FCSTD DOCUMENT  (FreeCAD 1.0R39319 (Git))
Label: Week1Sketch2
License: All rights reserved
LicenseURL: https://en.wikipedia.org/wiki/All_rights_reserved
objects: Sketcher::SketchObject×1, PartDesign::Body×1
note: 3 computed .brp shape members not serialized (recipe doc carries the construction recipe); baked Part::Feature solids carry a one-line shape summary decoded from their .brp

FEATURE [Sketcher::SketchObject] Sketch
  ArcFitTolerance = 1e-06
  AttachmentSupport = -> [XY_Plane]
  FullyConstrained = true
  MakeInternals = false
  MapMode = 5
  sketch-geometry (30):
    g0: ArcOfCircle CenterX=0 CenterY=0 CenterZ=0 NormalX=0 NormalY=0 NormalZ=1 AngleXU=0 Radius=55 StartAngle=0.182835 EndAngle=1.38796
    g1: ArcOfCircle CenterX=-112.5 CenterY=0 CenterZ=0 NormalX=0 NormalY=0 NormalZ=1 AngleXU=0 Radius=26 StartAngle=0.394791 EndAngle=5.88839
    g2: ArcOfCircle CenterX=112.5 CenterY=0 CenterZ=0 NormalX=0 NormalY=0 NormalZ=1 AngleXU=0 Radius=26 StartAngle=3.53638 EndAngle=9.02999
    g3: Circle [constr] CenterX=0 CenterY=0 CenterZ=0 NormalX=0 NormalY=0 NormalZ=1 AngleXU=0 Radius=112.5
    g4: ArcOfCircle CenterX=0 CenterY=112.5 CenterZ=0 NormalX=0 NormalY=0 NormalZ=1 AngleXU=0 Radius=26 StartAngle=5.10718 EndAngle=10.6008
    g5: ArcOfCircle CenterX=0 CenterY=-112.5 CenterZ=0 NormalX=0 NormalY=0 NormalZ=1 AngleXU=0 Radius=26 StartAngle=1.96559 EndAngle=7.45919
    g6: LineSegment StartX=-130.885 StartY=18.3848 StartZ=0 EndX=-18.3848 EndY=130.885 EndZ=0
    g7: LineSegment StartX=18.3848 StartY=130.885 StartZ=0 EndX=130.885 EndY=18.3848 EndZ=0
    g8: Circle CenterX=-112.5 CenterY=0 CenterZ=0 NormalX=0 NormalY=0 NormalZ=1 AngleXU=0 Radius=20
    g9: Circle CenterX=0 CenterY=112.5 CenterZ=0 NormalX=0 NormalY=0 NormalZ=1 AngleXU=0 Radius=20
    g10: Circle CenterX=112.5 CenterY=0 CenterZ=0 NormalX=0 NormalY=0 NormalZ=1 AngleXU=0 Radius=20
    g11: Circle CenterX=0 CenterY=-112.5 CenterZ=0 NormalX=0 NormalY=0 NormalZ=1 AngleXU=0 Radius=20
    g12: Circle CenterX=0 CenterY=0 CenterZ=0 NormalX=0 NormalY=0 NormalZ=1 AngleXU=0 Radius=44
    g13: LineSegment StartX=-95.1795 StartY=10 StartZ=0 EndX=-42.8486 EndY=10 EndZ=0
    g14: LineSegment StartX=-95.1795 StartY=-10 StartZ=0 EndX=-42.8486 EndY=-10 EndZ=0
    g15: LineSegment StartX=-10 StartY=95.1795 StartZ=0 EndX=-10 EndY=42.8486 EndZ=0
    g16: LineSegment StartX=10 StartY=95.1795 StartZ=0 EndX=10 EndY=42.8486 EndZ=0
    g17: LineSegment StartX=-10 StartY=-95.1795 StartZ=0 EndX=-10 EndY=-42.8486 EndZ=0
    g18: LineSegment StartX=10 StartY=-95.1795 StartZ=0 EndX=10 EndY=-42.8486 EndZ=0
    g19: LineSegment StartX=95.1795 StartY=10 StartZ=0 EndX=42.8486 EndY=10 EndZ=0
    g20: LineSegment StartX=95.1795 StartY=-10 StartZ=0 EndX=42.8486 EndY=-10 EndZ=0
    g21: ArcOfCircle CenterX=0 CenterY=0 CenterZ=0 NormalX=0 NormalY=0 NormalZ=1 AngleXU=0 Radius=55 StartAngle=1.75363 EndAngle=2.95876
    g22: ArcOfCircle CenterX=0 CenterY=0 CenterZ=0 NormalX=0 NormalY=0 NormalZ=1 AngleXU=0 Radius=55 StartAngle=3.32443 EndAngle=4.52955
    g23: ArcOfCircle CenterX=0 CenterY=0 CenterZ=0 NormalX=0 NormalY=0 NormalZ=1 AngleXU=0 Radius=55 StartAngle=4.89522 EndAngle=6.10035
    g24: ArcOfCircle CenterX=-84.9611 CenterY=-59.9801 CenterZ=0 NormalX=0 NormalY=0 NormalZ=1 AngleXU=0 Radius=40 StartAngle=0.614722 EndAngle=2.00122
    g25: ArcOfCircle CenterX=0 CenterY=0 CenterZ=0 NormalX=0 NormalY=0 NormalZ=1 AngleXU=0 Radius=64 StartAngle=3.75631 EndAngle=4.09767
    g26: ArcOfCircle CenterX=-59.9801 CenterY=-84.9611 CenterZ=0 NormalX=0 NormalY=0 NormalZ=1 AngleXU=0 Radius=40 StartAngle=5.85276 EndAngle=7.23926
    g27: ArcOfCircle CenterX=84.9611 CenterY=-59.9801 CenterZ=0 NormalX=0 NormalY=0 NormalZ=1 AngleXU=0 Radius=40 StartAngle=1.14037 EndAngle=2.52687
    g28: ArcOfCircle CenterX=0 CenterY=0 CenterZ=0 NormalX=0 NormalY=0 NormalZ=1 AngleXU=0 Radius=64 StartAngle=5.32711 EndAngle=5.66846
    g29: ArcOfCircle CenterX=59.9801 CenterY=-84.9611 CenterZ=0 NormalX=0 NormalY=0 NormalZ=1 AngleXU=0 Radius=40 StartAngle=2.18552 EndAngle=3.57202
  constraints (96):
    c: Coincident(g0,g-1)
    c: PointOnObject(g1,g-1)
    c: Diameter(g0) = 110
    c: Diameter(g1) = 52
    c: Equal(g1,g2)
    c: Coincident(g3,g0)
    c: Diameter(g3) = 225
    c: PointOnObject(g1,g3)
    c: PointOnObject(g2,g3)
    c: PointOnObject(g4,g-2)
    c: PointOnObject(g5,g-2)
    c: Equal(g1,g4)
    c: Equal(g4,g5)
    c: PointOnObject(g4,g3)
    c: PointOnObject(g5,g3)
    c: PointOnObject(g2,g-1)
    c: Tangent(g6,g4) = 1.5708
    c: Tangent(g6,g1) = 1.5708
    c: Tangent(g7,g4) = 1.5708
    c: Tangent(g7,g2) = 1.5708
    c: Coincident(g8,g1)
    c: Coincident(g9,g4)
    c: Coincident(g10,g2)
    c: Coincident(g11,g5)
    c: Diameter(g8) = 40
    c: Equal(g8,g9)
    c: Equal(g9,g10)
    c: Equal(g10,g11)
    c: Coincident(g12,g0)
    c: Diameter(g12) = 88
    c: PointOnObject(g13,g8)
    c: PointOnObject(g13,g12)
    c: Horizontal(g13)
    c: PointOnObject(g14,g8)
    c: PointOnObject(g14,g12)
    c: Horizontal(g14)
    c: Equal(g13,g14)
    c: Distance(g14,g13) = 20
    c: PointOnObject(g15,g9)
    c: PointOnObject(g15,g12)
    c: Vertical(g15)
    c: PointOnObject(g16,g9)
    c: PointOnObject(g16,g12)
    c: Vertical(g16)
    c: Equal(g15,g16)
    c: Distance(g16,g15) = 20
    c: Vertical(g17)
    c: Vertical(g18)
    c: Equal(g17,g18)
    c: Distance(g18,g17) = 20
    c: Horizontal(g19)
    c: Horizontal(g20)
    c: Equal(g19,g20)
    c: Distance(g20,g19) = 20
    c: Block(g18)
    c: Block(g17)
    c: Block(g19)
    c: Block(g20)
    c: PointOnObject(g1,g14)
    c: PointOnObject(g1,g13)
    c: PointOnObject(g4,g15)
    c: PointOnObject(g4,g16)
    c: PointOnObject(g2,g19)
    c: PointOnObject(g2,g20)
    c: PointOnObject(g23,g20)
    c: PointOnObject(g0,g19)
    c: Equal(g0,g21)
    c: PointOnObject(g0,g16)
    c: PointOnObject(g21,g15)
    c: Coincident(g0,g21)
    c: Equal(g21,g22)
    c: PointOnObject(g21,g13)
    c: PointOnObject(g22,g14)
    c: Coincident(g21,g22)
    c: Equal(g22,g23)
    c: PointOnObject(g22,g17)
    c: PointOnObject(g23,g18)
    c: Coincident(g22,g23)
    c: PointOnObject(g5,g18)
    c: PointOnObject(g5,g17)
    c: Tangent(g24,g25) = 1.5708
    c: Tangent(g25,g26) = 1.5708
    c: Coincident(g25,g0)
    c: Radius(g25) = 64
    c: Radius(g24) = 40
    c: Radius(g26) = 40
    c: Tangent(g24,g1) = 1.5708
    c: Tangent(g26,g5) = 1.5708
    c: Tangent(g27,g28) = 1.5708
    c: Tangent(g28,g29) = 1.5708
    c: Radius(g28) = 64
    c: Radius(g27) = 40
    c: Radius(g29) = 40
    c: Block(g29)
    c: Block(g28)
    c: Block(g27)
FEATURE [PartDesign::Body] Body
  AllowCompound = false
  Group = -> [Sketch]
  Origin = -> Origin
